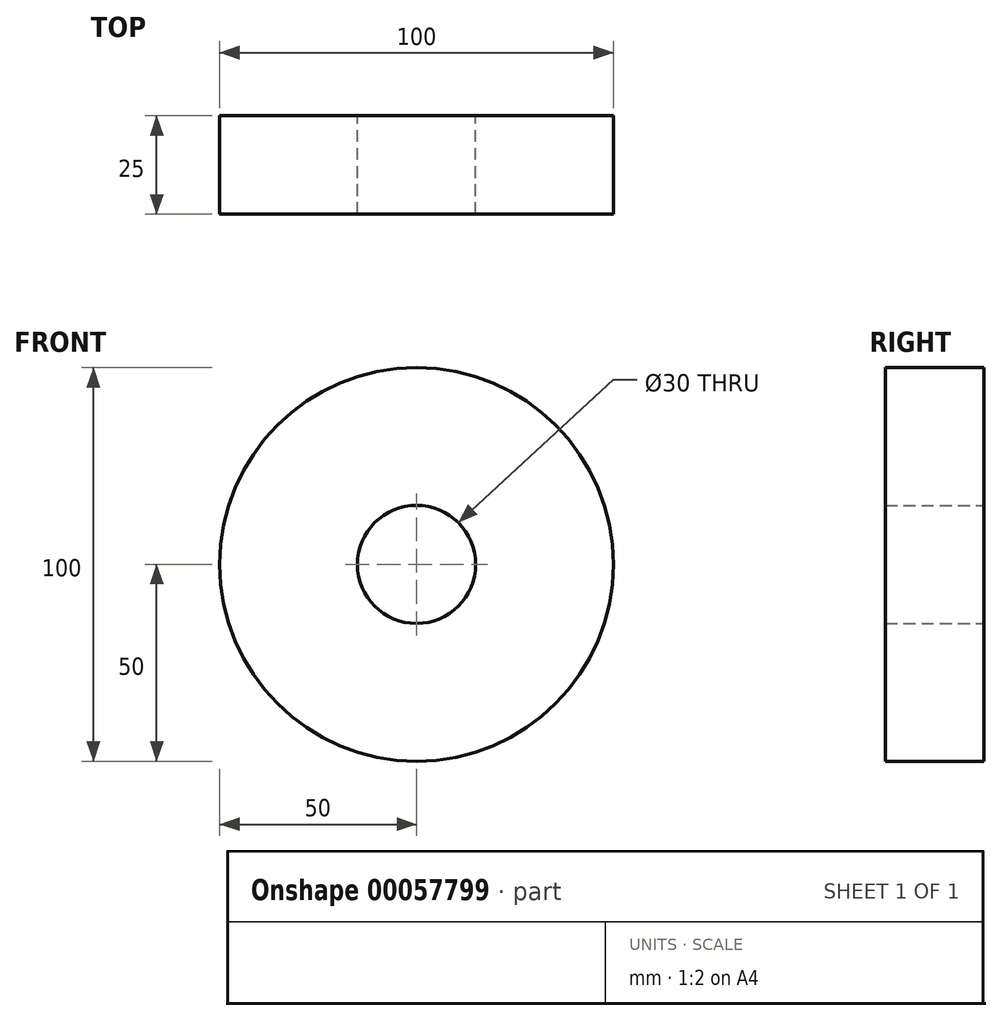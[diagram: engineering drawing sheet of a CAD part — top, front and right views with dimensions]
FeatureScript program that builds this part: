
annotation { "Feature Type Name" : "Feature", "Feature Type Description" : "" }
export const myFeature = defineFeature(function(context is Context, id is Id, definition is map)
    precondition{}
    {
        {
            var Q0;
            Q0=qCreatedBy(makeId("Front.planeOp"),FACE);
            var sketch = newSketch(context, id + "F0", { "sketchPlane" : qUnion([Q0])});
            skCircle(sketch, "E0", {"center": v(0, 0) * mm, "radius": 15 * mm});
            skCircle(sketch, "E1", {"center": v(0, 0) * mm, "radius": 50 * mm});
            skSolve(sketch);
        }
        {
            var Q0;
            Q0=makeQuery(id+"F0.imprint","IMPRINT",FACE,{"disambiguationData":[TD([[makeQuery(id+"F0.imprint","IMPRINT",EDGE,{"derivedFrom":sQuery(id+"F0.wireOp",EDGE,"E0")}),-1.0]])]});
            extrude(context, id + "F1", {"entities" : qUnion([Q0]), "depth" : 25 * mm});
        }
    });
